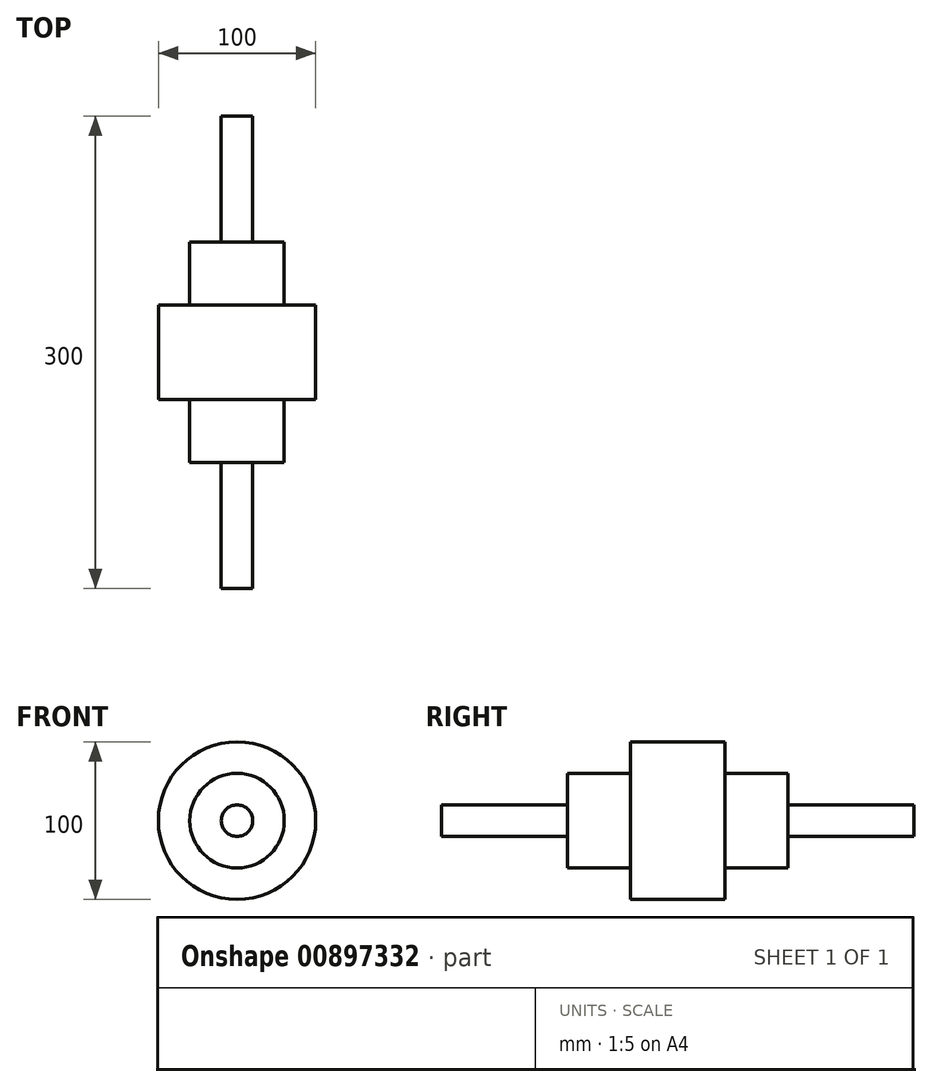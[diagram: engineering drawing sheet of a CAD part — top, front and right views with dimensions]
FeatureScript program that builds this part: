
annotation { "Feature Type Name" : "Feature", "Feature Type Description" : "" }
export const myFeature = defineFeature(function(context is Context, id is Id, definition is map)
    precondition{}
    {
        {
            var Q0;
            Q0=qCreatedBy(makeId("Front.planeOp"),FACE);
            var sketch = newSketch(context, id + "F0", { "sketchPlane" : qUnion([Q0])});
            skCircle(sketch, "E0", {"center": v(0, 0) * mm, "radius": 50 * mm});
            skSolve(sketch);
        }
        {
            var Q0;
            Q0=makeQuery(id+"F0.imprint","IMPRINT",FACE,{"disambiguationData":[TD([[makeQuery(id+"F0.imprint","IMPRINT",EDGE,{"derivedFrom":sQuery(id+"F0.wireOp",EDGE,"E0")}),1.0]])]});
            extrude(context, id + "F1", {"entities" : qUnion([Q0]), "depth" : 60 * mm, "offsetDistance" : 25.4 * mm});
        }
        {
            var Q0;
            Q0=makeQuery(id+"F1.opExtrude","CAP_FACE",FACE,{"disambiguationData":[OSD([sQuery(id+"F0.wireOp",EDGE,"E0")])],"isStart":false});
            var sketch = newSketch(context, id + "F2", { "sketchPlane" : qUnion([Q0])});
            skCircle(sketch, "E1", {"center": v(0, 0) * mm, "radius": 30 * mm});
            skSolve(sketch);
        }
        {
            var Q0;
            Q0=makeQuery(id+"F2.imprint","IMPRINT",FACE,{"disambiguationData":[TD([[makeQuery(id+"F2.imprint","IMPRINT",EDGE,{"derivedFrom":sQuery(id+"F2.wireOp",EDGE,"E1")}),1.0]])]});
            extrude(context, id + "F3", {"entities" : qUnion([Q0]), "operationType" : NewBodyOperationType.ADD, "depth" : 40 * mm, "offsetDistance" : 25.4 * mm});
        }
        {
            var Q0;
            Q0=makeQuery(id+"F3.opExtrude","CAP_FACE",FACE,{"disambiguationData":[OSD([sQuery(id+"F2.wireOp",EDGE,"E1")])],"isStart":false});
            var sketch = newSketch(context, id + "F4", { "sketchPlane" : qUnion([Q0])});
            skCircle(sketch, "E2", {"center": v(0, 0) * mm, "radius": 10 * mm});
            skSolve(sketch);
        }
        {
            var Q0;
            Q0=makeQuery(id+"F4.imprint","IMPRINT",FACE,{"disambiguationData":[TD([[makeQuery(id+"F4.imprint","IMPRINT",EDGE,{"derivedFrom":sQuery(id+"F4.wireOp",EDGE,"E2")}),1.0]])]});
            extrude(context, id + "F5", {"entities" : qUnion([Q0]), "operationType" : NewBodyOperationType.ADD, "depth" : 80 * mm, "offsetDistance" : 25.4 * mm});
        }
        {
            var Q0;
            Q0=makeQuery(id+"F1.opExtrude","CAP_FACE",FACE,{"disambiguationData":[OSD([sQuery(id+"F0.wireOp",EDGE,"E0")])],"isStart":true});
            var sketch = newSketch(context, id + "F6", { "sketchPlane" : qUnion([Q0])});
            skCircle(sketch, "E3", {"center": v(0, 0) * mm, "radius": 30 * mm});
            skSolve(sketch);
        }
        {
            var Q0;
            Q0=makeQuery(id+"F6.imprint","IMPRINT",FACE,{"disambiguationData":[TD([[makeQuery(id+"F6.imprint","IMPRINT",EDGE,{"derivedFrom":sQuery(id+"F6.wireOp",EDGE,"E3")}),1.0]])]});
            extrude(context, id + "F7", {"entities" : qUnion([Q0]), "operationType" : NewBodyOperationType.ADD, "depth" : 40 * mm, "offsetDistance" : 25.4 * mm});
        }
        {
            var Q0;
            Q0=makeQuery(id+"F7.opExtrude","CAP_FACE",FACE,{"disambiguationData":[OSD([sQuery(id+"F6.wireOp",EDGE,"E3")])],"isStart":false});
            var sketch = newSketch(context, id + "F8", { "sketchPlane" : qUnion([Q0])});
            skSolve(sketch);
        }
        {
            var Q0;
            Q0=makeQuery(id+"F8.imprint","IMPRINT",FACE,{"disambiguationData":[TD([[makeQuery(id+"F8.imprint","IMPRINT",EDGE,{"derivedFrom":makeQuery(id+"F7.opExtrude","CAP_EDGE",EDGE,{"disambiguationData":[OSD([sQuery(id+"F6.wireOp",EDGE,"E3")])],"isStart":false})}),1.0]])]});
            var sketch = newSketch(context, id + "F9", { "sketchPlane" : qUnion([Q0])});
            skCircle(sketch, "E4", {"center": v(0, 0) * mm, "radius": 10 * mm});
            skSolve(sketch);
        }
        {
            var Q0;
            Q0 = qSketchRegion(id + "F9", true);
            extrude(context, id + "F10", {"entities" : qUnion([Q0]), "operationType" : NewBodyOperationType.ADD, "depth" : 80 * mm, "offsetDistance" : 25.4 * mm});
        }
    });
